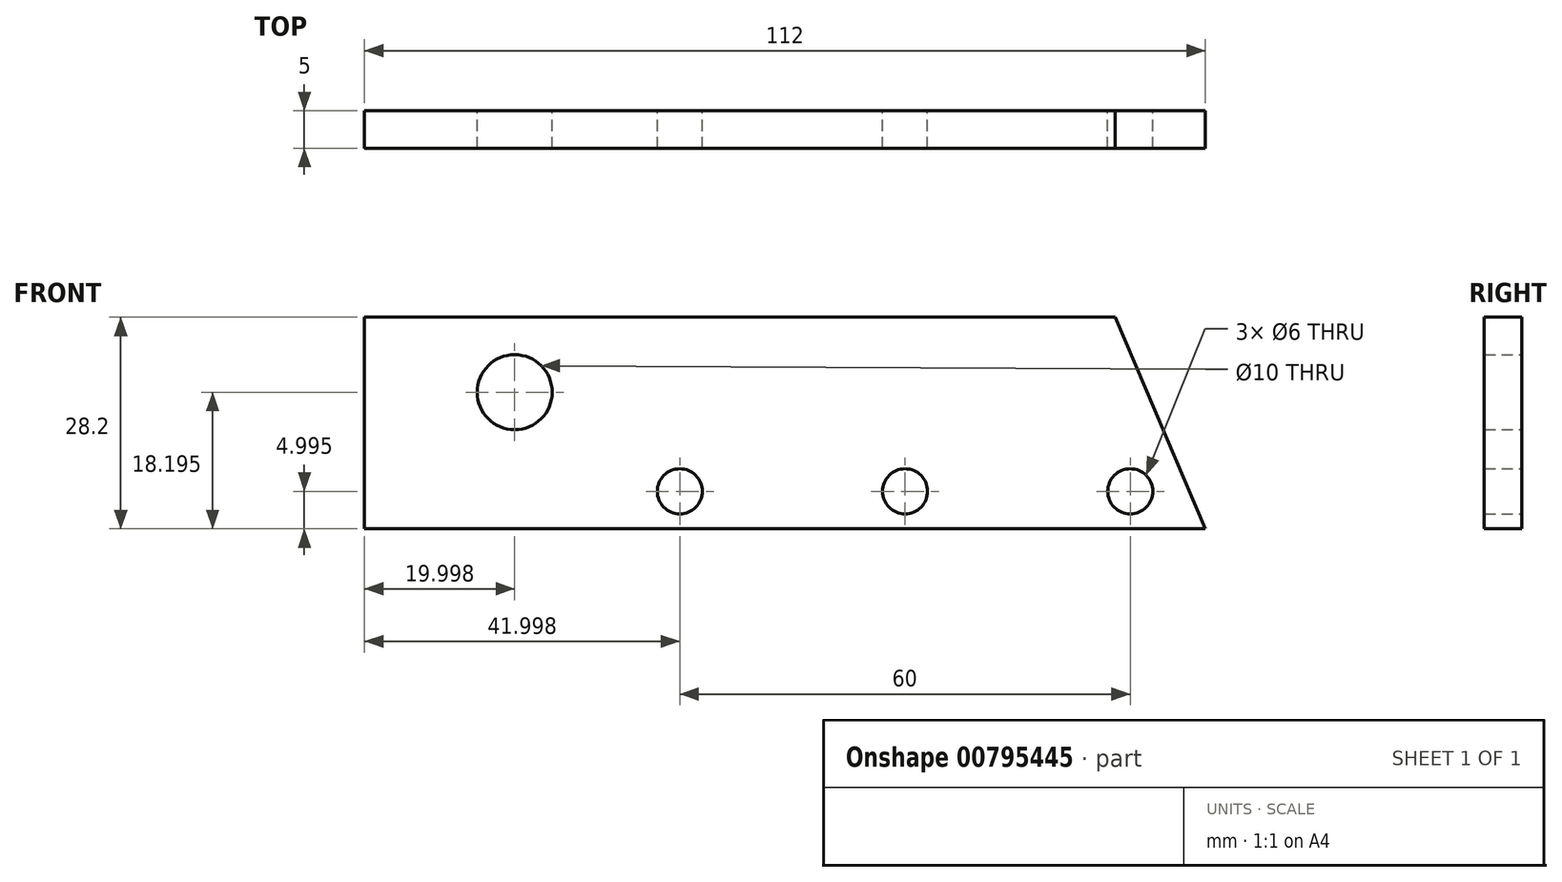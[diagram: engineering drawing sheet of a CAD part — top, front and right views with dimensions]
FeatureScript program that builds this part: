
annotation { "Feature Type Name" : "Feature", "Feature Type Description" : "" }
export const myFeature = defineFeature(function(context is Context, id is Id, definition is map)
    precondition{}
    {
        {
            var Q0;
            Q0=qCreatedBy(makeId("Front.planeOp"),FACE);
            var sketch = newSketch(context, id + "F0", { "sketchPlane" : qUnion([Q0])});
            skPoint(sketch, "E0.middle", {"position": v(0, 0) * mm});
            skPoint(sketch, "E1", {"position": v(-60.61, 15.84) * mm});
            skCircle(sketch, "E2", {"center": v(-60.61, 15.84) * mm, "radius": 5 * mm});
            skPoint(sketch, "E3", {"position": v(-80.61, 25.84) * mm});
            skLineSegment(sketch, "E4.bottom", {"start": v(31.39, -2.36) * mm, "end": v(-80.61, -2.36) * mm});
            skLineSegment(sketch, "E4.top", {"start": v(19.39, 25.84) * mm, "end": v(-80.61, 25.84) * mm});
            skLineSegment(sketch, "E4.right", {"start": v(-80.61, -2.36) * mm, "end": v(-80.61, 25.84) * mm});
            skPoint(sketch, "E5", {"position": v(19.39, 25.84) * mm});
            skPoint(sketch, "E6", {"position": v(31.39, -2.36) * mm});
            skLineSegment(sketch, "E7", {"start": v(19.39, 25.84) * mm, "end": v(31.39, -2.36) * mm});
            skPoint(sketch, "E8", {"position": v(-38.61, 2.64) * mm});
            skPoint(sketch, "E9", {"position": v(-8.61, 2.64) * mm});
            skPoint(sketch, "E10", {"position": v(21.39, 2.64) * mm});
            skCircle(sketch, "E11", {"center": v(-38.61, 2.64) * mm, "radius": 3 * mm});
            skCircle(sketch, "E12", {"center": v(-8.61, 2.64) * mm, "radius": 3 * mm});
            skCircle(sketch, "E13", {"center": v(21.39, 2.64) * mm, "radius": 3 * mm});
            skSolve(sketch);
        }
        {
            var Q0;
            Q0=makeQuery(id+"F0.imprint","IMPRINT",FACE,{"disambiguationData":[TD([[makeQuery(id+"F0.imprint","IMPRINT",EDGE,{"derivedFrom":sQuery(id+"F0.wireOp",EDGE,"E2")}),-1.0]])]});
            extrude(context, id + "F1", {"entities" : qUnion([Q0]), "depth" : 5 * mm, "offsetDistance" : 25 * mm});
        }
        {
            var Q0;
            Q0=makeQuery(id+"F1.opExtrude","SWEPT_FACE",FACE,{"disambiguationData":[OSD([sQuery(id+"F0.wireOp",EDGE,"E4.top")])]});
            extrude(context, id + "F2", {"entities" : qUnion([Q0]), "operationType" : NewBodyOperationType.REMOVE, "oppositeDirection" : true, "depth" : 2 * mm, "offsetDistance" : 25 * mm});
        }
        {
            var Q0;
            Q0=makeQuery(id+"F0.imprint","IMPRINT",FACE,{"disambiguationData":[TD([[makeQuery(id+"F0.imprint","IMPRINT",EDGE,{"derivedFrom":sQuery(id+"F0.wireOp",EDGE,"E2")}),-1.0]])]});
            extrude(context, id + "F3", {"entities" : qUnion([Q0]), "operationType" : NewBodyOperationType.ADD, "depth" : 5 * mm, "offsetDistance" : 25 * mm});
        }
    });
